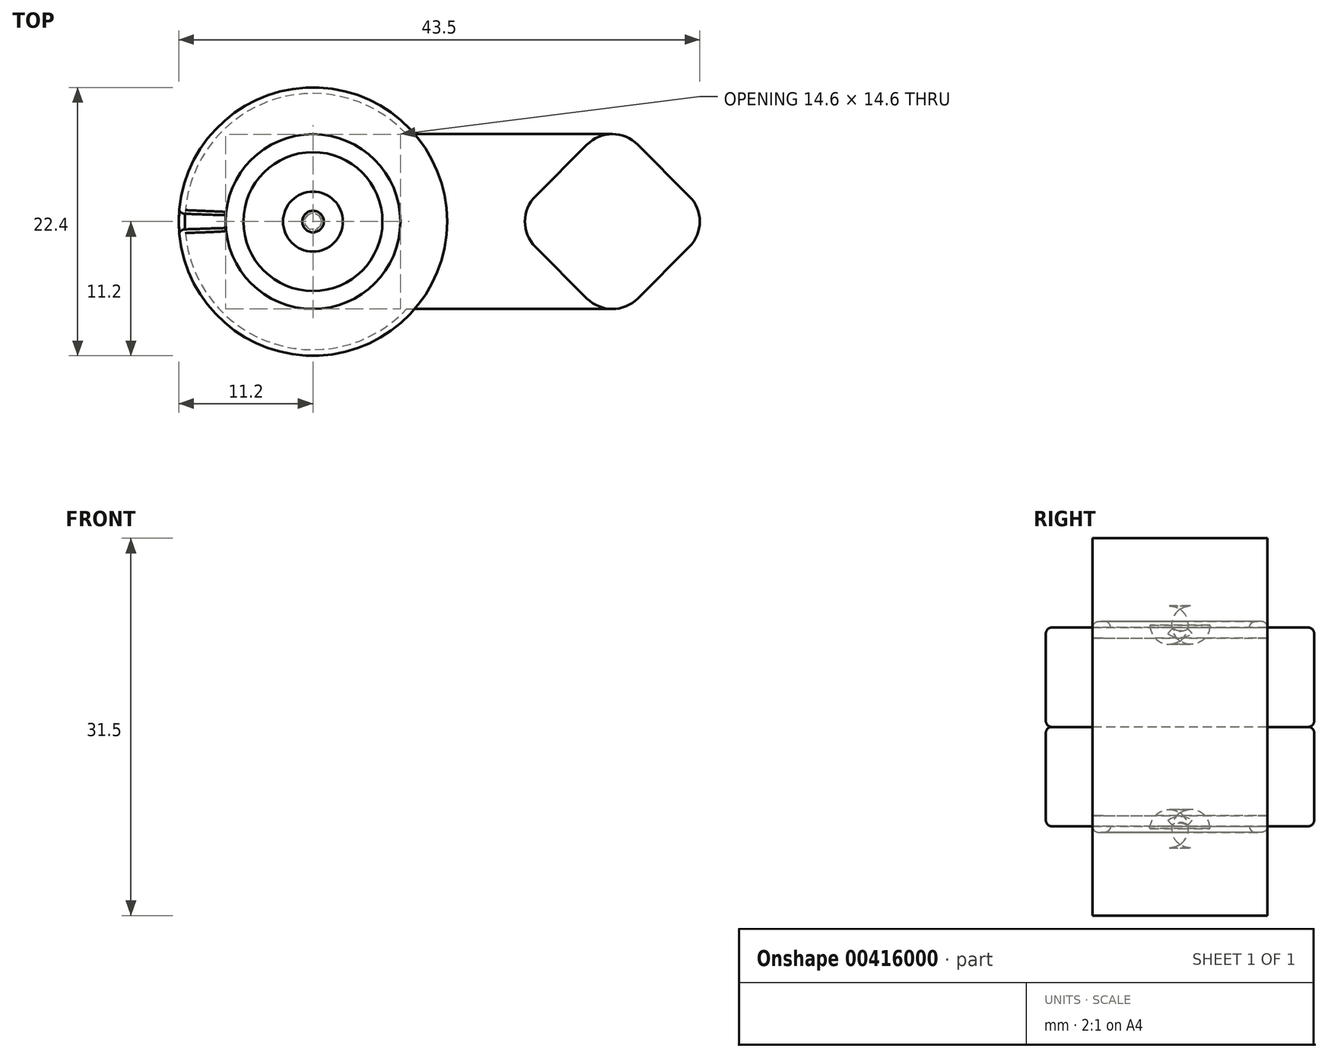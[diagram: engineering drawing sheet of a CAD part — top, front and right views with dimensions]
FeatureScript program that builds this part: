
annotation { "Feature Type Name" : "Feature", "Feature Type Description" : "" }
export const myFeature = defineFeature(function(context is Context, id is Id, definition is map)
    precondition{}
    {
        {
            var Q0;
            Q0=qCreatedBy(makeId("Front.planeOp"),FACE);
            var sketch = newSketch(context, id + "F0", { "sketchPlane" : qUnion([Q0])});
            skLineSegment(sketch, "E0", {"start": v(0, 0) * mm, "end": v(0, 8.3) * mm});
            skLineSegment(sketch, "E1", {"start": v(-11.2, 8.3) * mm, "end": v(-11.2, 5.9) * mm});
            skLineSegment(sketch, "E2", {"start": v(-7.3, 0) * mm, "end": v(0, 0) * mm});
            skLineSegment(sketch, "E3", {"start": v(-11.2, 8.3) * mm, "end": v(-7.3, 8.3) * mm});
            skLineSegment(sketch, "E4", {"start": v(-7.3, 8.3) * mm, "end": v(-7.3, 8.8) * mm});
            skLineSegment(sketch, "E5", {"start": v(-7.3, 8.8) * mm, "end": v(-5.8, 8.8) * mm});
            skLineSegment(sketch, "E6", {"start": v(-5.8, 8.8) * mm, "end": v(-5.8, 8.3) * mm});
            skLineSegment(sketch, "E7", {"start": v(-5.8, 8.3) * mm, "end": v(0, 8.3) * mm});
            skLineSegment(sketch, "E8", {"start": v(0, 8.3) * mm, "end": v(0, 10.1) * mm});
            skLineSegment(sketch, "E9", {"start": v(0, 10.1) * mm, "end": v(-0.9, 10.1) * mm});
            skLineSegment(sketch, "E10", {"start": v(-2.5, 8.5) * mm, "end": v(-2.5, 8.3) * mm});
            skPoint(sketch, "E11.visualSharp", {"position": v(-7.3, 0) * mm});
            skLineSegment(sketch, "E11.filletArc", {"start": v(-7.3, 0) * mm, "end": v(-7.3, 0) * mm});
            skPoint(sketch, "E12.visualSharp", {"position": v(-2.5, 10.1) * mm});
            skArc(sketch, "E12.filletArc", {"start": v(-0.9, 10.1) * mm, "mid": v(-2.03, 9.63) * mm, "end": v(-2.5, 8.5) * mm});
            skLineSegment(sketch, "E13", {"start": v(-11.2, 5.9) * mm, "end": v(-11.2, 0) * mm});
            skLineSegment(sketch, "E14", {"start": v(-11.2, 0) * mm, "end": v(-7.3, 0) * mm});
            skSolve(sketch);
        }
        {
            var Q0;
            Q0=makeQuery(id+"F0.imprint","IMPRINT",FACE,{"disambiguationData":[TD([[makeQuery(id+"F0.imprint","IMPRINT",EDGE,{"derivedFrom":sQuery(id+"F0.wireOp",EDGE,"E0")}),1.0]])]});
            var Q1;
            {var subQ1=sQuery(id+"F0.wireOp",EDGE,"E8");Q1=makeQuery(id+"F0.imprint","IMPRINT",FACE,{"disambiguationData":[TD([[makeQuery(id+"F0.imprint","IMPRINT",EDGE,{"derivedFrom":subQ1}),1.0]])]});}
            var Q2;
            Q2=sQuery(id+"F0.wireOp",EDGE,"E0");
            revolve(context, id + "F1", {"entities" : qUnion([Q0, Q1]), "axis" : qUnion([Q2]), "revolveType" : RevolveType.FULL});
        }
        {
            var Q0;
            Q0=qCreatedBy(makeId("Front.planeOp"),FACE);
            var sketch = newSketch(context, id + "F2", { "sketchPlane" : qUnion([Q0])});
            skLineSegment(sketch, "E15", {"start": v(0, 0) * mm, "end": v(0, 9) * mm, "construction": true});
            skLineSegment(sketch, "E16", {"start": v(0, 9) * mm, "end": v(-11.2, 9) * mm});
            skLineSegment(sketch, "E17", {"start": v(-11.2, 9) * mm, "end": v(-11.2, 7.95) * mm});
            skLineSegment(sketch, "E18", {"start": v(-11.2, 7.95) * mm, "end": v(-7.3, 8.05) * mm});
            skLineSegment(sketch, "E19", {"start": v(-7.3, 8.05) * mm, "end": v(-7.3, 9) * mm});
            skSolve(sketch);
        }
        {
            var Q0;
            {var subQ0=sQuery(id+"F2.wireOp",EDGE,"E17");Q0=makeQuery(id+"F2.imprint","IMPRINT",FACE,{"disambiguationData":[TD([[makeQuery(id+"F2.imprint","IMPRINT",EDGE,{"derivedFrom":subQ0}),1.0]])]});}
            var Q1;
            Q1=sQuery(id+"F2.wireOp",EDGE,"E16");
            revolve(context, id + "F3", {"operationType" : NewBodyOperationType.REMOVE, "entities" : qUnion([Q0]), "axis" : qUnion([Q1]), "revolveType" : RevolveType.FULL, "oppositeDirection" : true});
        }
        {
            var Q0;
            Q0=makeQuery(id+"F3.boolean.opBoolean","INTERSECT",EDGE,{"disambiguationData":[OD(1.0)],"derivedFrom":[makeQuery(id+"F1.opRevolve","SWEPT_FACE",FACE,{"disambiguationData":[OSD([sQuery(id+"F0.wireOp",EDGE,"E3")])]}),makeQuery(id+"F3.opRevolve","SWEPT_FACE",FACE,{"disambiguationData":[OSD([sQuery(id+"F2.wireOp",EDGE,"E18")])]})]});
            var Q1;
            Q1=makeQuery(id+"F3.boolean.opBoolean","INTERSECT",EDGE,{"disambiguationData":[OD(0.0)],"derivedFrom":[makeQuery(id+"F1.opRevolve","SWEPT_FACE",FACE,{"disambiguationData":[OSD([sQuery(id+"F0.wireOp",EDGE,"E3")])]}),makeQuery(id+"F3.opRevolve","SWEPT_FACE",FACE,{"disambiguationData":[OSD([sQuery(id+"F2.wireOp",EDGE,"E18")])]})]});
            fillet(context, id + "F4", {"entities" : qUnion([Q0, Q1]), "radius" : 0.5 * mm, "tangentPropagation" : true, "allowEdgeOverflow" : false});
        }
        {
            var Q0;
            Q0=makeQuery(id+"F1.opRevolve","SWEPT_FACE",FACE,{"disambiguationData":[OSD([sQuery(id+"F0.wireOp",EDGE,"E1")])]});
            var Q1;
            Q1=makeQuery(id+"F1.opRevolve","SWEPT_FACE",FACE,{"disambiguationData":[OSD([sQuery(id+"F0.wireOp",EDGE,"E5")])]});
            fillet(context, id + "F5", {"entities" : qUnion([Q0, Q1]), "radius" : 0.5 * mm, "tangentPropagation" : true, "allowEdgeOverflow" : false});
        }
        {
            var Q0;
            Q0=qCreatedBy(makeId("Top.planeOp"),FACE);
            var sketch = newSketch(context, id + "F6", { "sketchPlane" : qUnion([Q0])});
            skCircle(sketch, "E20", {"center": v(0, 0) * mm, "radius": 7.3 * mm, "construction": true});
            skLineSegment(sketch, "E21.bottom", {"start": v(0, -7.3) * mm, "end": v(25, -7.3) * mm});
            skLineSegment(sketch, "E21.top", {"start": v(0, 7.3) * mm, "end": v(25, 7.3) * mm});
            skLineSegment(sketch, "E21.left", {"start": v(0, -7.3) * mm, "end": v(0, 7.3) * mm});
            skLineSegment(sketch, "E21.right", {"start": v(25, -7.3) * mm, "end": v(25, 7.3) * mm});
            skLineSegment(sketch, "E22.bottom", {"start": v(31.42, -2.12) * mm, "end": v(27.12, -6.42) * mm});
            skLineSegment(sketch, "E22.top", {"start": v(22.88, 6.42) * mm, "end": v(18.58, 2.12) * mm});
            skLineSegment(sketch, "E22.left", {"start": v(31.42, 2.12) * mm, "end": v(27.12, 6.42) * mm});
            skLineSegment(sketch, "E22.right", {"start": v(22.88, -6.42) * mm, "end": v(18.58, -2.12) * mm});
            skPoint(sketch, "E22.middle", {"position": v(25, 0) * mm});
            skPoint(sketch, "E23.visualSharp", {"position": v(25, -8.54) * mm});
            skArc(sketch, "E23.filletArc", {"start": v(22.88, -6.42) * mm, "mid": v(25, -7.3) * mm, "end": v(27.12, -6.42) * mm});
            skPoint(sketch, "E24.visualSharp", {"position": v(33.54, 0) * mm});
            skArc(sketch, "E24.filletArc", {"start": v(31.42, -2.12) * mm, "mid": v(32.3, 0) * mm, "end": v(31.42, 2.12) * mm});
            skPoint(sketch, "E25.visualSharp", {"position": v(25, 8.54) * mm});
            skArc(sketch, "E25.filletArc", {"start": v(27.12, 6.42) * mm, "mid": v(25, 7.3) * mm, "end": v(22.88, 6.42) * mm});
            skPoint(sketch, "E26.visualSharp", {"position": v(16.46, 0) * mm});
            skArc(sketch, "E26.filletArc", {"start": v(18.58, 2.12) * mm, "mid": v(17.7, 0) * mm, "end": v(18.58, -2.12) * mm});
            skLineSegment(sketch, "E27", {"start": v(16.46, 0) * mm, "end": v(33.54, 0) * mm, "construction": true});
            skLineSegment(sketch, "E28", {"start": v(25, -8.54) * mm, "end": v(25, 8.54) * mm, "construction": true});
            skSolve(sketch);
        }
        {
            var Q0;
            {var subQ4=sQuery(id+"F6.wireOp",EDGE,"E21.bottom");Q0=makeQuery(id+"F6.imprint","IMPRINT",FACE,{"disambiguationData":[TD([[makeQuery(id+"F6.imprint","IMPRINT",EDGE,{"derivedFrom":subQ4}),1.0]])]});}
            extrude(context, id + "F7", {"entities" : qUnion([Q0]), "operationType" : NewBodyOperationType.ADD, "depth" : 7.4 * mm});
        }
        {
            var Q0;
            {var subQ2=sQuery(id+"F6.wireOp",EDGE,"E21.right");Q0=makeQuery(id+"F6.imprint","IMPRINT",FACE,{"disambiguationData":[TD([[makeQuery(id+"F6.imprint","IMPRINT",EDGE,{"derivedFrom":subQ2}),-1.0]])]});}
            var Q1;
            {var subQ3=sQuery(id+"F6.wireOp",EDGE,"E21.right");Q1=makeQuery(id+"F6.imprint","IMPRINT",FACE,{"disambiguationData":[TD([[makeQuery(id+"F6.imprint","IMPRINT",EDGE,{"derivedFrom":subQ3}),1.0]])]});}
            extrude(context, id + "F8", {"entities" : qUnion([Q0, Q1]), "operationType" : NewBodyOperationType.ADD, "depth" : (31.5 / 2) * mm});
        }
        {
            var Q0;
            Q0=makeQuery(id+"F1.opRevolve","SWEPT_BODY",BODY,{"disambiguationData":[OSD([sQuery(id+"F0.wireOp",EDGE,"E0"),sQuery(id+"F0.wireOp",EDGE,"E1"),sQuery(id+"F0.wireOp",EDGE,"3asSoTjZ-X1Kf-mMLV-8St3-GEXtygtMqkNr"),sQuery(id+"F0.wireOp",EDGE,"u4Z3KoIV-1xI6-Y3ZN-PIDE-9BeYEG5ibkun"),sQuery(id+"F0.wireOp",EDGE,"E2"),sQuery(id+"F0.wireOp",EDGE,"E3"),sQuery(id+"F0.wireOp",EDGE,"E4"),sQuery(id+"F0.wireOp",EDGE,"E5"),sQuery(id+"F0.wireOp",EDGE,"E6"),sQuery(id+"F0.wireOp",EDGE,"E7"),sQuery(id+"F0.wireOp",EDGE,"E8"),sQuery(id+"F0.wireOp",EDGE,"E9"),sQuery(id+"F0.wireOp",EDGE,"E10"),sQuery(id+"F0.wireOp",EDGE,"E12.filletArc")])]});
            var Q1;
            Q1=qCreatedBy(makeId("Top.planeOp"),FACE);
            mirror(context, id + "F9", {"operationType" : NewBodyOperationType.ADD, "entities" : qUnion([Q0]), "mirrorPlane" : qUnion([Q1])});
        }
    });
